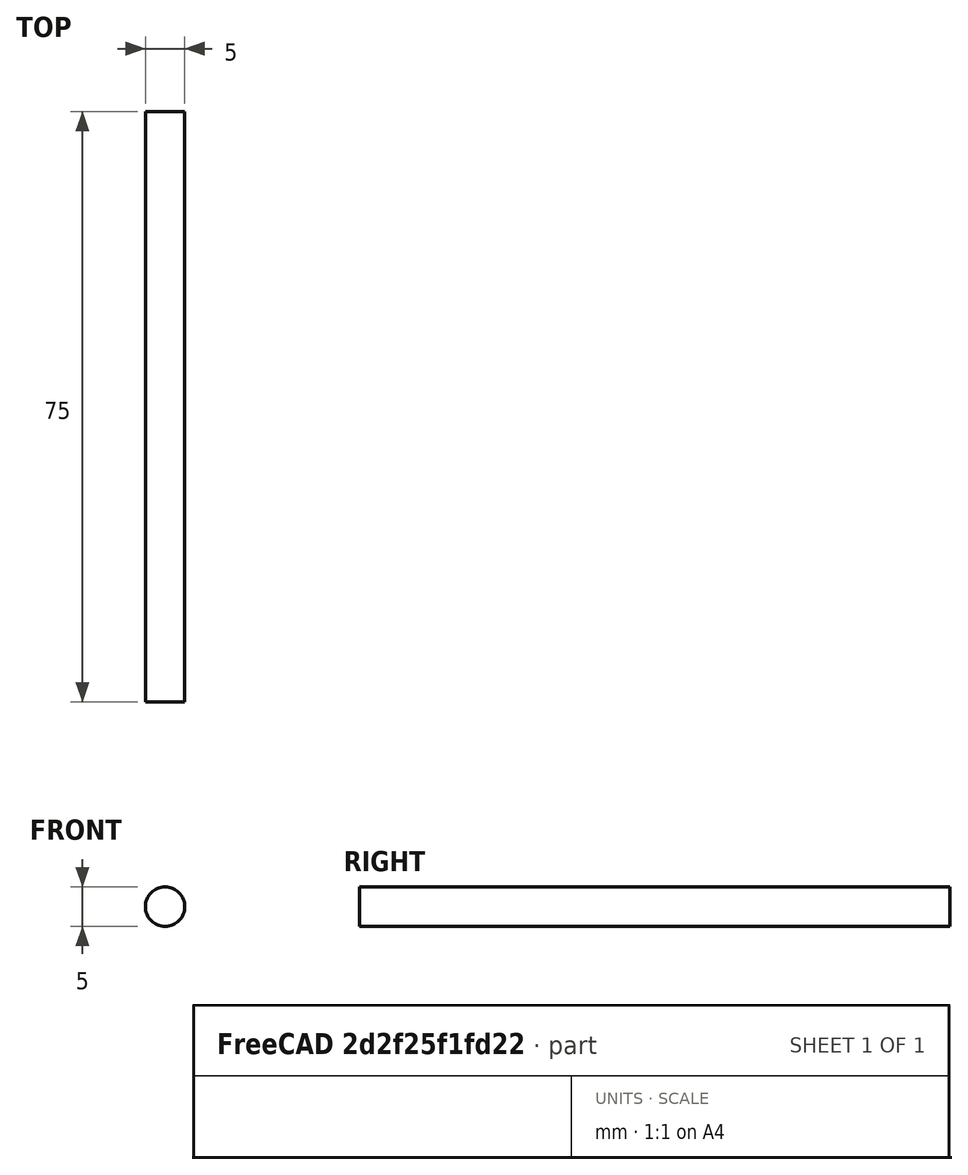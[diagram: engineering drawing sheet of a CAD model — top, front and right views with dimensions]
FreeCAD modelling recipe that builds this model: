
FCSTD DOCUMENT  (FreeCAD 1.0R39109 (Git))
Label: Stange-DerGerät
License: All rights reserved
LicenseURL: https://en.wikipedia.org/wiki/All_rights_reserved
objects: Sketcher::SketchObject×1, PartDesign::Pad×1, PartDesign::Body×1
note: 6 computed .brp shape members not serialized (recipe doc carries the construction recipe); baked Part::Feature solids carry a one-line shape summary decoded from their .brp

FEATURE [Sketcher::SketchObject] Sketch
  ArcFitTolerance = 1e-06
  AttachmentSupport = -> [XZ_Plane]
  FullyConstrained = true
  MakeInternals = false
  MapMode = 5
  Placement = pos=(0,0,0) rot=(1,0,0;1.5708rad)
  sketch-geometry (1):
    g0: Circle CenterX=0 CenterY=0 CenterZ=0 NormalX=0 NormalY=0 NormalZ=1 AngleXU=0 Radius=2.5
  constraints (2):
    c: Diameter(g0) = 5
    c: Coincident(g0,g-1)
FEATURE [PartDesign::Pad] Pad
  Direction = (0,-1,2e-16)
  Length = 75
  Length2 = 10
  Placement = pos=(0,0,0) rot=(1,0,0;1.5708rad)
  Profile = -> Sketch
  ReferenceAxis = -> Sketch [N_Axis]
  Refine = true
  Suppressed = false
  Type = 0
FEATURE [PartDesign::Body] Body  label="Körper"
  AllowCompound = false
  Group = -> [Sketch,Pad]
  Origin = -> Origin
  Tip = -> Pad
